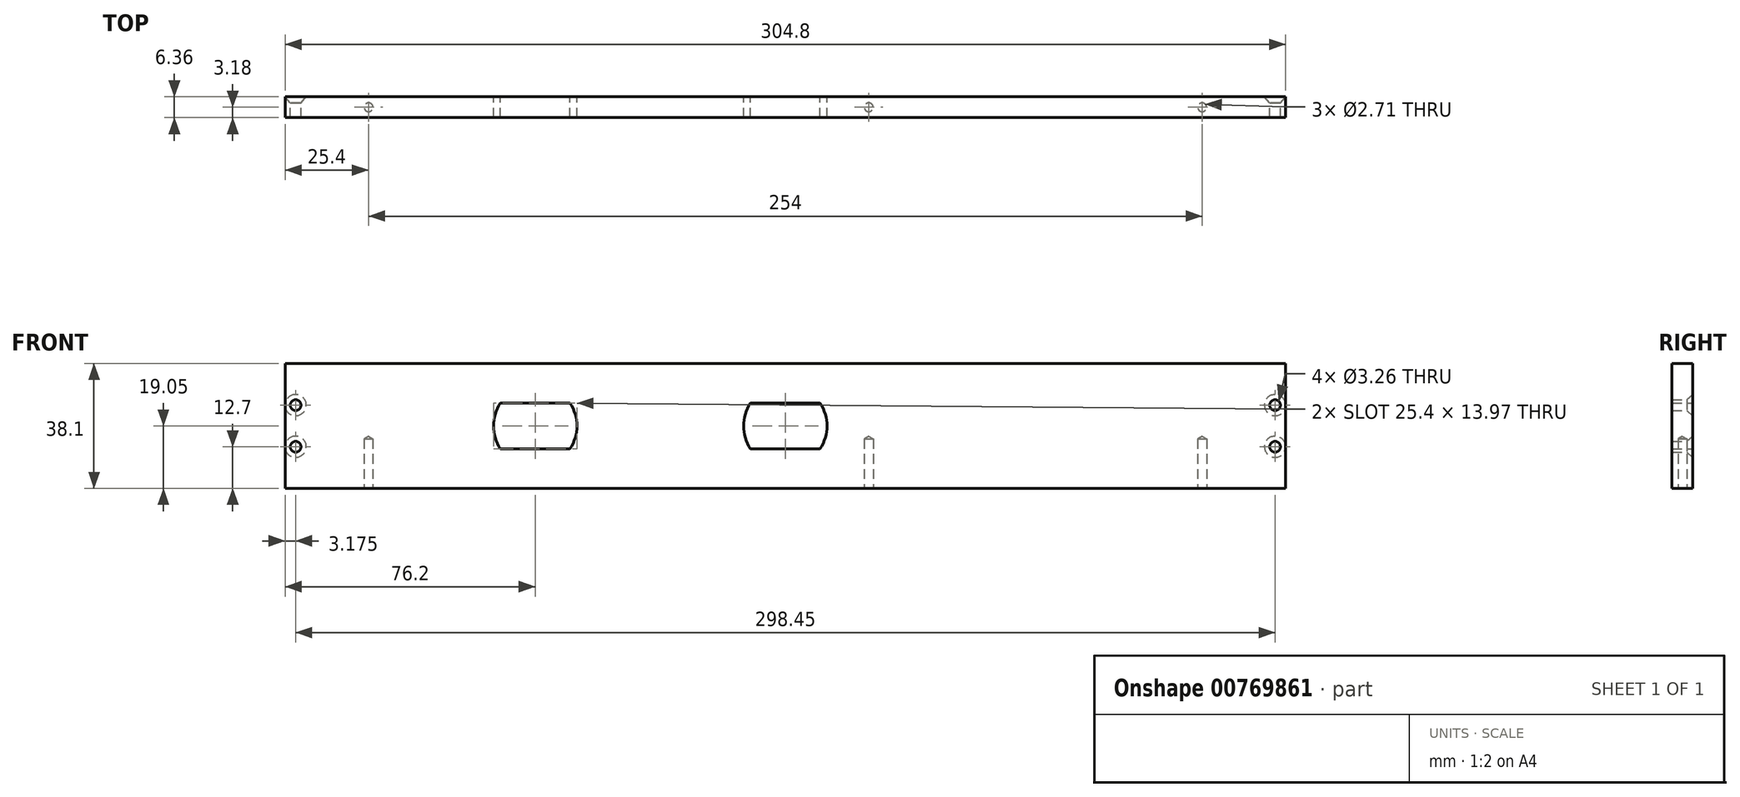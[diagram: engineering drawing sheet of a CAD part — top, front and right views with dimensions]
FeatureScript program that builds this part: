
annotation { "Feature Type Name" : "Feature", "Feature Type Description" : "" }
export const myFeature = defineFeature(function(context is Context, id is Id, definition is map)
    precondition{}
    {
        {
            var Q0;
            Q0=qCreatedBy(makeId("Top.planeOp"),FACE);
            var sketch = newSketch(context, id + "F0", { "sketchPlane" : qUnion([Q0])});
            skLineSegment(sketch, "E0.bottom", {"start": v(-152.4, 3.17) * mm, "end": v(152.4, 3.17) * mm});
            skLineSegment(sketch, "E0.top", {"start": v(-152.4, -3.18) * mm, "end": v(152.4, -3.18) * mm});
            skLineSegment(sketch, "E0.left", {"start": v(-152.4, 3.17) * mm, "end": v(-152.4, -3.18) * mm});
            skLineSegment(sketch, "E0.right", {"start": v(152.4, 3.17) * mm, "end": v(152.4, -3.18) * mm});
            skLineSegment(sketch, "E1", {"start": v(-152.4, 3.17) * mm, "end": v(152.4, -3.17) * mm, "construction": true});
            skSolve(sketch);
        }
        {
            var Q0;
            Q0 = qSketchRegion(id + "F0", true);
            extrude(context, id + "F1", {"entities" : qUnion([Q0]), "depth" : 38.1 * mm, "offsetDistance" : 25.4 * mm});
        }
        {
            var Q0;
            Q0=makeQuery(id+"F1.opExtrude","CAP_FACE",FACE,{"disambiguationData":[OSD([sQuery(id+"F0.wireOp",EDGE,"E0.bottom"),sQuery(id+"F0.wireOp",EDGE,"E0.top"),sQuery(id+"F0.wireOp",EDGE,"E0.left"),sQuery(id+"F0.wireOp",EDGE,"E0.right")])],"isStart":true});
            var sketch = newSketch(context, id + "F2", { "sketchPlane" : qUnion([Q0])});
            skLineSegment(sketch, "E2", {"start": v(-152.4, 0) * mm, "end": v(152.4, 0) * mm, "construction": true});
            skPoint(sketch, "E3", {"position": v(-127, 0) * mm});
            skPoint(sketch, "E4", {"position": v(25.4, 0) * mm});
            skPoint(sketch, "E5", {"position": v(127, 0) * mm});
            skSolve(sketch);
        }
        {
            var Q0;
            Q0=sQuery(id+"F2.wireOp",VERTEX,"E3");
            var Q1;
            Q1=sQuery(id+"F2.wireOp",VERTEX,"E5");
            var Q2;
            Q2=sQuery(id+"F2.wireOp",VERTEX,"E4");
            var Q3;
            Q3=makeQuery(id+"F1.opExtrude","SWEPT_BODY",BODY,{"disambiguationData":[OSD([sQuery(id+"F0.wireOp",EDGE,"E0.bottom"),sQuery(id+"F0.wireOp",EDGE,"E0.top"),sQuery(id+"F0.wireOp",EDGE,"E0.left"),sQuery(id+"F0.wireOp",EDGE,"E0.right")])]});
            hole(context, id + "F3", {"style" : HoleStyle.SIMPLE, "endStyle" : HoleEndStyle.BLIND, "standardTappedOrClearance" : lookupTablePath({ "standard" : "ANSI", "engagement" : "75%", "pitch" : "32 tpi", "size" : "#6", "type" : "Tapped" }), "standardBlindInLast" : lookupTablePath({ "standard" : "ANSI", "engagement" : "75%", "pitch" : "32 tpi", "size" : "#6", "type" : "Tapped" }), "holeDiameter" : 2.7 * mm, "majorDiameter" : 3.5 * mm, "showTappedDepth" : true, "holeDepth" : 15.08 * mm, "tappedDepth" : 12.7 * mm, "tapClearance" : 3, "locations" : qUnion([Q0, Q1, Q2]), "scope" : qUnion([Q3])});
        }
        {
            var Q0;
            Q0=makeQuery(id+"F1.opExtrude","SWEPT_FACE",FACE,{"disambiguationData":[OSD([sQuery(id+"F0.wireOp",EDGE,"E0.bottom")])]});
            var sketch = newSketch(context, id + "F4", { "sketchPlane" : qUnion([Q0])});
            skLineSegment(sketch, "E6", {"start": v(-149.22, 38.1) * mm, "end": v(-149.22, 0) * mm, "construction": true});
            skLineSegment(sketch, "E7", {"start": v(149.22, 38.1) * mm, "end": v(149.22, 0) * mm, "construction": true});
            skPoint(sketch, "E8", {"position": v(-149.22, 25.4) * mm});
            skPoint(sketch, "E9", {"position": v(-149.22, 19.05) * mm});
            skPoint(sketch, "E10", {"position": v(-149.22, 12.7) * mm});
            skPoint(sketch, "E11", {"position": v(149.22, 19.05) * mm});
            skPoint(sketch, "E12", {"position": v(149.22, 25.4) * mm});
            skPoint(sketch, "E13", {"position": v(149.22, 12.7) * mm});
            skSolve(sketch);
        }
        {
            var Q0;
            Q0=sQuery(id+"F4.wireOp",VERTEX,"E8");
            var Q1;
            Q1=sQuery(id+"F4.wireOp",VERTEX,"E10");
            var Q2;
            Q2=sQuery(id+"F4.wireOp",VERTEX,"E12");
            var Q3;
            Q3=sQuery(id+"F4.wireOp",VERTEX,"E13");
            var Q4;
            Q4=makeQuery(id+"F1.opExtrude","SWEPT_BODY",BODY,{"disambiguationData":[OSD([sQuery(id+"F0.wireOp",EDGE,"E0.bottom"),sQuery(id+"F0.wireOp",EDGE,"E0.top"),sQuery(id+"F0.wireOp",EDGE,"E0.left"),sQuery(id+"F0.wireOp",EDGE,"E0.right")])]});
            hole(context, id + "F5", {"style" : HoleStyle.C_SINK, "endStyle" : HoleEndStyle.THROUGH, "standardTappedOrClearance" : lookupTablePath({ "standard" : "ANSI", "fit" : "Normal (ASME)", "size" : "#4", "type" : "Clearance" }), "standardBlindInLast" : lookupTablePath({ "fit" : "Free", "standard" : "ANSI", "size" : "#4", "type" : "Clearance" }), "holeDiameter" : 3.26 * mm, "cSinkDiameter" : 6.48 * mm, "cSinkAngle" : 82 * degree, "majorDiameter" : 6.35 * mm, "tappedDepth" : 11.84 * mm, "tapClearance" : 3, "startFromSketch" : true, "locations" : qUnion([Q0, Q1, Q2, Q3]), "scope" : qUnion([Q4])});
        }
        {
            var Q0;
            Q0=makeQuery(id+"F1.opExtrude","SWEPT_FACE",FACE,{"disambiguationData":[OSD([sQuery(id+"F0.wireOp",EDGE,"E0.bottom")])]});
            var sketch = newSketch(context, id + "F6", { "sketchPlane" : qUnion([Q0])});
            skLineSegment(sketch, "E14", {"start": v(-152.4, 19.05) * mm, "end": v(152.4, 19.05) * mm, "construction": true});
            skArc(sketch, "E15", {"start": v(-10.6, 26.04) * mm, "mid": v(-12.7, 19.05) * mm, "end": v(-10.6, 12.07) * mm});
            skArc(sketch, "E16", {"start": v(86.8, 12.07) * mm, "mid": v(88.9, 19.05) * mm, "end": v(86.8, 26.04) * mm});
            skLineSegment(sketch, "E17.bottom", {"start": v(-10.6, 26.04) * mm, "end": v(10.6, 26.04) * mm});
            skLineSegment(sketch, "E17.top", {"start": v(-10.6, 12.07) * mm, "end": v(10.6, 12.07) * mm});
            skLineSegment(sketch, "E17.left", {"start": v(-10.6, 26.04) * mm, "end": v(-10.6, 12.07) * mm, "construction": true});
            skLineSegment(sketch, "E17.right", {"start": v(10.6, 26.04) * mm, "end": v(10.6, 12.07) * mm, "construction": true});
            skLineSegment(sketch, "E18.bottom", {"start": v(65.6, 26.04) * mm, "end": v(86.8, 26.04) * mm});
            skLineSegment(sketch, "E18.top", {"start": v(65.6, 12.07) * mm, "end": v(86.8, 12.07) * mm});
            skLineSegment(sketch, "E18.left", {"start": v(65.6, 26.04) * mm, "end": v(65.6, 12.07) * mm, "construction": true});
            skLineSegment(sketch, "E18.right", {"start": v(86.8, 26.04) * mm, "end": v(86.8, 12.07) * mm, "construction": true});
            skArc(sketch, "E19.trimOffspring", {"start": v(10.6, 12.07) * mm, "mid": v(12.7, 19.05) * mm, "end": v(10.6, 26.04) * mm});
            skArc(sketch, "E20.trimOffspring", {"start": v(65.6, 26.04) * mm, "mid": v(63.5, 19.05) * mm, "end": v(65.6, 12.07) * mm});
            skSolve(sketch);
        }
        {
            var Q0;
            Q0 = qSketchRegion(id + "F6", true);
            extrude(context, id + "F7", {"entities" : qUnion([Q0]), "operationType" : NewBodyOperationType.REMOVE, "oppositeDirection" : true, "depth" : 25.4 * mm, "offsetDistance" : 25.4 * mm});
        }
    });
